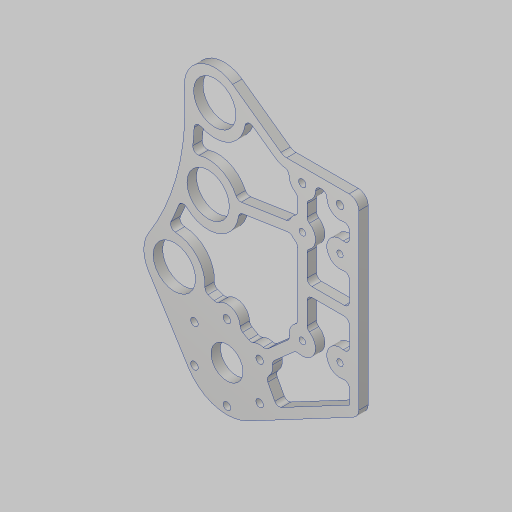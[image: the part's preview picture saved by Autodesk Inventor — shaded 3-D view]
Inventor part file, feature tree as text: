
AUTODESK INVENTOR PART (.ipt)
format: ipt  version: 2023.5 (Build 275446000, 446)  size: 437,248 bytes
history: native  units: in
note: dims shown in document units (in); Inventor stores cm internally (conversion verified against a paired STEP export)
features: sketch x4, hole x3, extrude x2, fillet x2, projected_geometry x2
ambient origin geometry x8: Origin, YZ Plane, XZ Plane, XY Plane, X Axis, Y Axis, Z Axis, Center Point
bodies: Solid1 (feature_tree)
feature tree (13):
  sketch  "Sketch1"  dims[d0=2.0in d1=15.0in]
  sketch  "Sketch2"  dims[d2=0.875in d3=17.0in]
  extrude  "Extrusion1"  Depth=2.0in
  hole  "Hole1"  [1 undecoded]
  hole  "Hole2"  [1 undecoded]
  fillet  "Fillet1"  Radius=1.0in
  hole  "Hole3"  [1 undecoded]
  extrude  "Extrusion2"  Depth=0.25in
  fillet  "Fillet2"  Radius=3.6in
  sketch  "Sketch3"  dims[d4=2.0in d5=17.0in d6=1.0in]
  projected_geometry  "Projected Loop1"
  sketch  "Sketch4"  dims[d7=0.2405in d8=2.4in d9=0.5in d10=3.6in d11=1.5in d12=1.5in d13=0.9in d14=3.7in d15=1.0in d16=3.4in d17=3.0in d20=2.0in d22=1.125in d23=4.297in d24=0.25in d25=2.0in d26=2.3622in d28=360.0deg d30=7.0in d31=2.0in d32=0.201in d33=1.0in d34=1.5in d35=1.0in d36=0.201in d37=1.0in d38=1.0in d39=2.5in d40=0.25in d41=0.0in d42=0.85in d43=0.201in d44=0.75in d45=0.385in d46=0.25in d47=0.5635in d48=1.0in d49=0.8108in d50=0.375in d51=0.171in d52=0.432in d53=0.385in d54=0.25in d55=0.5635in d56=1.0in d57=0.8108in d58=0.26in d59=1.825in d60=0.25in d61=0.25in d62=0.25in d63=1.0in d64=0.125in d65=0.125in d66=0.125in d67=0.125in d68=0.125in d69=0.125in d70=1.0in d71=0.0in d72=0.13in d74=1.75in d75=0.875in d76=0.156in d77=0.38in d78=0.375in d79=0.25in d80=0.5635in d81=1.0in d82=0.8108in d83=0.125in d84=0.125in]
  projected_geometry  "Projected Loop2"
note: 3 required parameter values undecoded (feature->parameter linkage not recoverable at this tier; creation-order binding heuristic only, values carry confidence <= 0.55)
